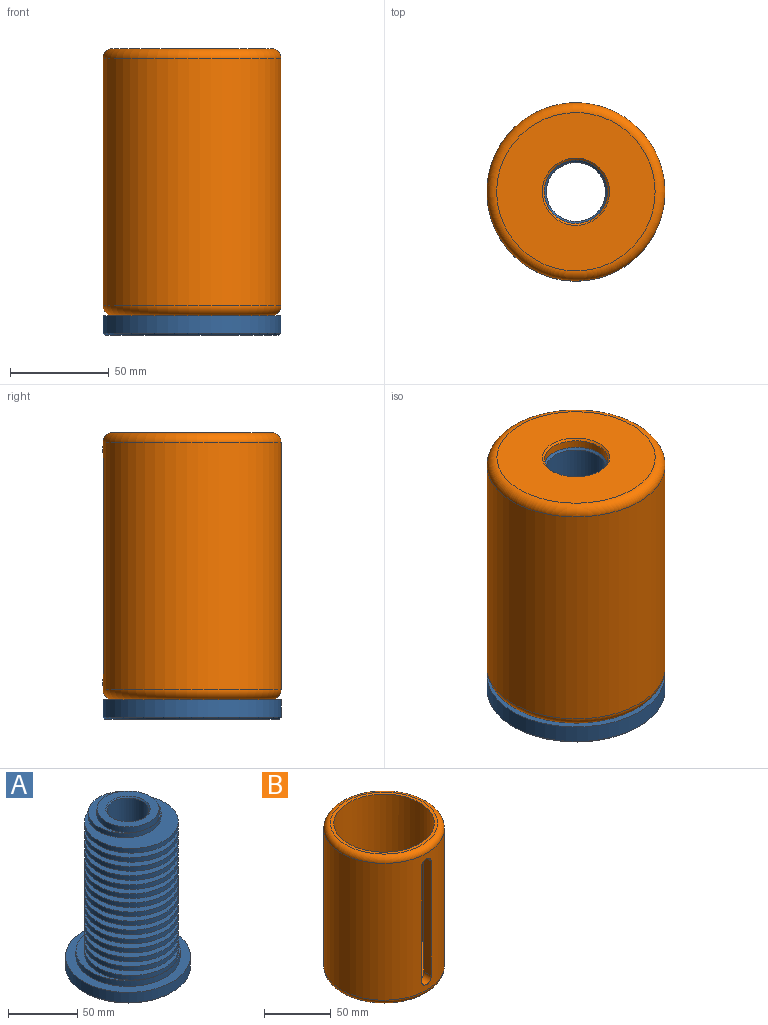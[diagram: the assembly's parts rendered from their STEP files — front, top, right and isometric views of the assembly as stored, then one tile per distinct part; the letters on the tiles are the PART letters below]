
ASSEMBLY  parts=2 mates=1
PART A: 71 faces, bbox 90x90x140 mm
  f0: cylinder r=33.75mm len=67.5mm, axis (0,0,-1), area 848.2mm2, adj f1,f2
  f1: plane 67.5x67.5mm, normal (0,0,1), area 1422mm2, adj f0,f35
  f2: plane 67.5x67.5mm, normal (0,0,-1), area 1422mm2, adj f0,f3
  f3: cylinder r=26.2mm len=52.4mm, axis (0,0,-1), area 658.5mm2, adj f2,f34
  f4: plane 88x88mm, normal (0,0,-1), area 5277.9mm2, adj f68,f70
  f5: cylinder r=45mm len=90mm, axis (0,0,-1), area 2544.7mm2, adj f6,f70
  f6: plane 90x90mm, normal (0,0,1), area 1943.9mm2, adj f5,f7
  f7: cylinder r=37.5mm len=75mm, axis (0,0,-1), area 1178.1mm2, adj f6,f8
  f8: plane 75x75mm, normal (0,0,1), area 839.4mm2, adj f7,f9
  f9: cylinder r=33.75mm len=67.5mm, axis (0,0,-1), area 848.2mm2, adj f8,f10
  f10: plane 67.5x67.5mm, normal (0,0,1), area 1422mm2, adj f9,f11
  f11: cylinder r=26.2mm len=52.4mm, axis (0,0,-1), area 658.5mm2, adj f10,f12
  f12: plane 67.5x67.5mm, normal (0,0,-1), area 1422mm2, adj f11,f13
  f13: cylinder r=33.75mm len=67.5mm, axis (0,0,-1), area 848.2mm2, adj f12,f14
  f14: plane 67.5x67.5mm, normal (0,0,1), area 1422mm2, adj f13,f15
  f15: cylinder r=26.2mm len=52.4mm, axis (0,0,-1), area 658.5mm2, adj f14,f16
  f16: plane 67.5x67.5mm, normal (0,0,-1), area 1422mm2, adj f15,f17
  f17: cylinder r=33.75mm len=67.5mm, axis (0,0,-1), area 848.2mm2, adj f16,f18
  f18: plane 67.5x67.5mm, normal (0,0,1), area 1422mm2, adj f17,f19
  f19: cylinder r=26.2mm len=52.4mm, axis (0,0,-1), area 658.5mm2, adj f18,f20
  f20: plane 67.5x67.5mm, normal (0,0,-1), area 1422mm2, adj f19,f21
  f21: cylinder r=33.75mm len=67.5mm, axis (0,0,-1), area 848.2mm2, adj f20,f22
  f22: plane 67.5x67.5mm, normal (0,0,1), area 1422mm2, adj f21,f23
  f23: cylinder r=26.2mm len=52.4mm, axis (0,0,-1), area 658.5mm2, adj f22,f24
  f24: plane 67.5x67.5mm, normal (0,0,-1), area 1422mm2, adj f23,f25
  f25: cylinder r=33.75mm len=67.5mm, axis (0,0,-1), area 848.2mm2, adj f24,f26
  f26: plane 67.5x67.5mm, normal (0,0,1), area 1422mm2, adj f25,f27
  f27: cylinder r=26.2mm len=52.4mm, axis (0,0,-1), area 658.5mm2, adj f26,f28
  f28: plane 67.5x67.5mm, normal (0,0,-1), area 1422mm2, adj f27,f29
  f29: cylinder r=33.75mm len=67.5mm, axis (0,0,-1), area 848.2mm2, adj f28,f30
  f30: plane 67.5x67.5mm, normal (0,0,1), area 1422mm2, adj f29,f31
  f31: cylinder r=26.2mm len=52.4mm, axis (0,0,-1), area 658.5mm2, adj f30,f32
  f32: plane 67.5x67.5mm, normal (0,0,-1), area 1422mm2, adj f31,f33
  f33: cylinder r=33.75mm len=67.5mm, axis (0,0,-1), area 848.2mm2, adj f32,f34
  f34: plane 67.5x67.5mm, normal (0,0,1), area 1422mm2, adj f3,f33
  f35: cylinder r=26.2mm len=52.4mm, axis (0,0,-1), area 658.5mm2, adj f1,f38
  f36: plane 67.5x67.5mm, normal (0,0,1), area 1422mm2, adj f37,f39
  f37: cylinder r=33.75mm len=67.5mm, axis (0,0,-1), area 848.2mm2, adj f36,f38
  f38: plane 67.5x67.5mm, normal (0,0,-1), area 1422mm2, adj f35,f37
  f39: cylinder r=26.2mm len=52.4mm, axis (0,0,-1), area 658.5mm2, adj f36,f42
  f40: plane 67.5x67.5mm, normal (0,0,1), area 1422mm2, adj f41,f43
  f41: cylinder r=33.75mm len=67.5mm, axis (0,0,-1), area 848.2mm2, adj f40,f42
  f42: plane 67.5x67.5mm, normal (0,0,-1), area 1422mm2, adj f39,f41
  f43: cylinder r=26.2mm len=52.4mm, axis (0,0,-1), area 658.5mm2, adj f40,f46
  f44: plane 67.5x67.5mm, normal (0,0,1), area 1422mm2, adj f45,f47
  f45: cylinder r=33.75mm len=67.5mm, axis (0,0,-1), area 848.2mm2, adj f44,f46
  f46: plane 67.5x67.5mm, normal (0,0,-1), area 1422mm2, adj f43,f45
  f47: cylinder r=26.2mm len=52.4mm, axis (0,0,-1), area 658.5mm2, adj f44,f50
  f48: plane 67.5x67.5mm, normal (0,0,1), area 1422mm2, adj f49,f51
  f49: cylinder r=33.75mm len=67.5mm, axis (0,0,-1), area 848.2mm2, adj f48,f50
  f50: plane 67.5x67.5mm, normal (0,0,-1), area 1422mm2, adj f47,f49
  f51: cylinder r=26.2mm len=52.4mm, axis (0,0,-1), area 658.5mm2, adj f48,f54
  f52: plane 67.5x67.5mm, normal (0,0,1), area 1422mm2, adj f53,f55
  f53: cylinder r=33.75mm len=67.5mm, axis (0,0,-1), area 848.2mm2, adj f52,f54
  f54: plane 67.5x67.5mm, normal (0,0,-1), area 1422mm2, adj f51,f53
  f55: cylinder r=26.2mm len=52.4mm, axis (0,0,-1), area 658.5mm2, adj f52,f58
  f56: plane 67.5x67.5mm, normal (0,0,1), area 1422mm2, adj f57,f59
  f57: cylinder r=33.75mm len=67.5mm, axis (0,0,-1), area 848.2mm2, adj f56,f58
  f58: plane 67.5x67.5mm, normal (0,0,-1), area 1422mm2, adj f55,f57
  f59: cylinder r=26.2mm len=52.4mm, axis (0,0,-1), area 658.5mm2, adj f56,f62
  f60: plane 67.5x67.5mm, normal (0,0,1), area 1422mm2, adj f61,f63
  f61: cylinder r=33.75mm len=67.5mm, axis (0,0,-1), area 848.2mm2, adj f60,f62
  f62: plane 67.5x67.5mm, normal (0,0,-1), area 1422mm2, adj f59,f61
  f63: cylinder r=26.2mm len=52.4mm, axis (0,0,-1), area 658.5mm2, adj f60,f64
  f64: plane 52.4x52.4mm, normal (0,0,1), area 580.2mm2, adj f63,f66
  f65: plane 44.8x44.8mm, normal (0,0,1), area 772.1mm2, adj f66,f69
  f66: cylinder r=22.4mm len=44.8mm, axis (0,0,-1), area 703.7mm2, adj f64,f65
  f67: cylinder r=15mm len=138mm, axis (0,0,-1), area 13006.2mm2, adj f68,f69
  f68: cone r=15mm half-angle=45deg, axis (0,0,-1), area 137.7mm2, adj f4,f67
  f69: cone r=15mm half-angle=45deg, axis (0,0,1), area 137.7mm2, adj f65,f67
  f70: cone r=45mm half-angle=45deg, axis (0,0,1), area 395.4mm2, adj f4,f5
PART B: 15 faces, bbox 97.4x97.4x135 mm
  f0: cylinder r=16mm len=32mm, axis (0,0,-1), area 402.1mm2, adj f7,f14
  f1: cylinder r=45mm len=125mm, axis (0,0,-1), area 34212.1mm2, adj f8,f9,f10,f11,f12,f13
  f2: plane 80x80mm, normal (0,0,1), area 608.7mm2, adj f4,f13
  f3: plane 80x80mm, normal (0,0,-1), area 4118.6mm2, adj f12,f14
  f4: cylinder r=37.5mm len=125mm, axis (0,0,1), area 28320.6mm2, adj f2,f5,f8,f9,f10,f11
  f5: plane 75x75mm, normal (0,0,1), area 2827.4mm2, adj f4,f6
  f6: cylinder r=22.5mm len=45mm, axis (0,0,1), area 706.9mm2, adj f5,f7
  f7: plane 45x45mm, normal (0,0,1), area 786.2mm2, adj f0,f6
  f8: plane 105x7.56mm, normal (1,0,0), area 793.4mm2, adj f1,f4,f10,f11
  f9: plane 105x7.56mm, normal (-1,0,0), area 793.4mm2, adj f1,f4,f10,f11
  f10: cylinder r=5mm len=10mm, axis (0,-1,0), area 118.2mm2, adj f1,f4,f8,f9
  f11: cylinder r=5mm len=10mm, axis (0,-1,0), area 118.2mm2, adj f1,f4,f8,f9
  f12: torus R=40mm, axis (0,0,1), area 2131mm2, adj f1,f3
  f13: torus R=40mm, axis (0,0,1), area 2131mm2, adj f1,f2
  f14: cone r=16mm half-angle=45deg, axis (0,0,-1), area 146.6mm2, adj f0,f3
PLACE A t=(-74.2,-6.55,-15.33)mm
PLACE B rot(axis=(1,0,0),180deg) t=(-74.2,-6.55,129.67)mm
MATE revolute B.f4 <-> A.f5  axis (0,0,-1) through (-74.2,-6.55,-5.33)mm
